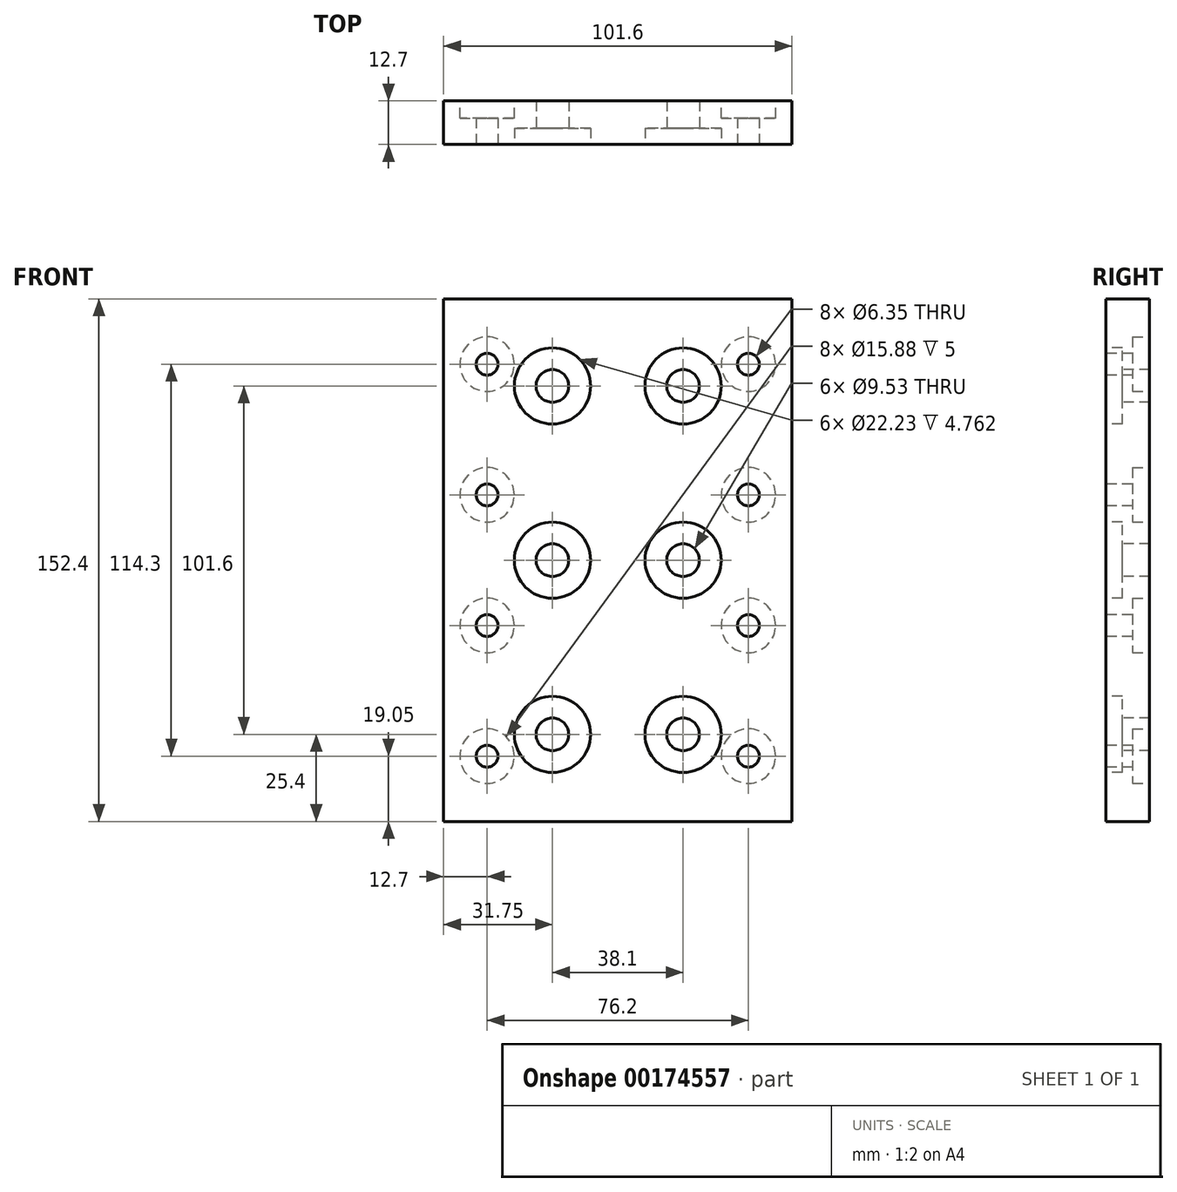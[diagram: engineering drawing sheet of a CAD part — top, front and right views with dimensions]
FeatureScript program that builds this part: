
annotation { "Feature Type Name" : "Feature", "Feature Type Description" : "" }
export const myFeature = defineFeature(function(context is Context, id is Id, definition is map)
    precondition{}
    {
        {
            var Q0;
            Q0=qCreatedBy(makeId("Front.planeOp"),FACE);
            var sketch = newSketch(context, id + "F0", { "sketchPlane" : qUnion([Q0])});
            skLineSegment(sketch, "E0.bottom", {"start": v(-50.8, -76.2) * mm, "end": v(50.8, -76.2) * mm});
            skLineSegment(sketch, "E0.top", {"start": v(-50.8, 76.2) * mm, "end": v(50.8, 76.2) * mm});
            skLineSegment(sketch, "E0.left", {"start": v(-50.8, -76.2) * mm, "end": v(-50.8, 76.2) * mm});
            skLineSegment(sketch, "E0.right", {"start": v(50.8, -76.2) * mm, "end": v(50.8, 76.2) * mm});
            skPoint(sketch, "E0.middle", {"position": v(0, 0) * mm});
            skSolve(sketch);
        }
        {
            var Q0;
            Q0 = qSketchRegion(id + "F0", true);
            extrude(context, id + "F1", {"entities" : qUnion([Q0]), "depth" : 12.7 * mm});
        }
        {
            var Q0;
            Q0=makeQuery(id+"F1.opExtrude","CAP_FACE",FACE,{"disambiguationData":[OSD([sQuery(id+"F0.wireOp",EDGE,"E0.bottom"),sQuery(id+"F0.wireOp",EDGE,"E0.top"),sQuery(id+"F0.wireOp",EDGE,"E0.left"),sQuery(id+"F0.wireOp",EDGE,"E0.right")])],"isStart":false});
            var sketch = newSketch(context, id + "F2", { "sketchPlane" : qUnion([Q0])});
            skLineSegment(sketch, "E1", {"start": v(-38.1, 57.15) * mm, "end": v(-50.8, 57.15) * mm, "construction": true});
            skCircle(sketch, "E2", {"center": v(-38.1, 57.15) * mm, "radius": 3.18 * mm});
            skCircle(sketch, "E3.0.1.0", {"center": v(-38.1, 19.05) * mm, "radius": 3.18 * mm});
            skCircle(sketch, "E3.0.2.0", {"center": v(-38.1, -19.05) * mm, "radius": 3.18 * mm});
            skCircle(sketch, "E3.0.3.0", {"center": v(-38.1, -57.15) * mm, "radius": 3.18 * mm});
            skCircle(sketch, "E3.1.0.0", {"center": v(38.1, 57.15) * mm, "radius": 3.18 * mm});
            skCircle(sketch, "E3.1.1.0", {"center": v(38.1, 19.05) * mm, "radius": 3.18 * mm});
            skCircle(sketch, "E3.1.2.0", {"center": v(38.1, -19.05) * mm, "radius": 3.18 * mm});
            skCircle(sketch, "E3.1.3.0", {"center": v(38.1, -57.15) * mm, "radius": 3.18 * mm});
            skLineSegment(sketch, "E3.direction1", {"start": v(-38.1, 57.15) * mm, "end": v(38.1, 57.15) * mm, "construction": true});
            skLineSegment(sketch, "E3.direction2", {"start": v(-38.1, 57.15) * mm, "end": v(-38.1, 19.05) * mm, "construction": true});
            skLineSegment(sketch, "E4", {"start": v(38.1, -57.15) * mm, "end": v(-38.1, -57.15) * mm, "construction": true});
            skLineSegment(sketch, "E5", {"start": v(0, -57.15) * mm, "end": v(0, -76.2) * mm, "construction": true});
            skLineSegment(sketch, "E6", {"start": v(0, 57.15) * mm, "end": v(0, 76.2) * mm, "construction": true});
            skSolve(sketch);
        }
        {
            var Q0;
            Q0 = qSketchRegion(id + "F2", true);
            extrude(context, id + "F3", {"entities" : qUnion([Q0]), "operationType" : NewBodyOperationType.REMOVE, "endBound" : BoundingType.THROUGH_ALL, "oppositeDirection" : true, "depth" : 25 * mm});
        }
        {
            var Q0;
            Q0=makeQuery(id+"F1.opExtrude","CAP_FACE",FACE,{"disambiguationData":[OSD([sQuery(id+"F0.wireOp",EDGE,"E0.bottom"),sQuery(id+"F0.wireOp",EDGE,"E0.top"),sQuery(id+"F0.wireOp",EDGE,"E0.left"),sQuery(id+"F0.wireOp",EDGE,"E0.right")])],"isStart":true});
            var sketch = newSketch(context, id + "F4", { "sketchPlane" : qUnion([Q0])});
            skCircle(sketch, "E7.0", {"center": v(-38.1, 57.15) * mm, "radius": 7.94 * mm});
            skCircle(sketch, "E8.0.1.0", {"center": v(-38.1, 19.05) * mm, "radius": 7.94 * mm});
            skCircle(sketch, "E8.0.2.0", {"center": v(-38.1, -19.05) * mm, "radius": 7.94 * mm});
            skCircle(sketch, "E8.0.3.0", {"center": v(-38.1, -57.15) * mm, "radius": 7.94 * mm});
            skCircle(sketch, "E8.1.0.0", {"center": v(38.1, 57.15) * mm, "radius": 7.94 * mm});
            skCircle(sketch, "E8.1.1.0", {"center": v(38.1, 19.05) * mm, "radius": 7.94 * mm});
            skCircle(sketch, "E8.1.2.0", {"center": v(38.1, -19.05) * mm, "radius": 7.94 * mm});
            skCircle(sketch, "E8.1.3.0", {"center": v(38.1, -57.15) * mm, "radius": 7.94 * mm});
            skLineSegment(sketch, "E8.direction1", {"start": v(-38.1, 57.15) * mm, "end": v(38.1, 57.15) * mm, "construction": true});
            skLineSegment(sketch, "E8.direction2", {"start": v(-38.1, 57.15) * mm, "end": v(-38.1, 19.05) * mm, "construction": true});
            skSolve(sketch);
        }
        {
            var Q0;
            Q0 = qSketchRegion(id + "F4", true);
            extrude(context, id + "F5", {"entities" : qUnion([Q0]), "operationType" : NewBodyOperationType.REMOVE, "oppositeDirection" : true, "depth" : 5 * mm});
        }
        {
            var Q0;
            Q0=makeQuery(id+"F1.opExtrude","CAP_FACE",FACE,{"disambiguationData":[OSD([sQuery(id+"F0.wireOp",EDGE,"E0.bottom"),sQuery(id+"F0.wireOp",EDGE,"E0.top"),sQuery(id+"F0.wireOp",EDGE,"E0.left"),sQuery(id+"F0.wireOp",EDGE,"E0.right")])],"isStart":false});
            var sketch = newSketch(context, id + "F6", { "sketchPlane" : qUnion([Q0])});
            skLineSegment(sketch, "E9", {"start": v(-19.05, 76.2) * mm, "end": v(-19.05, 50.8) * mm, "construction": true});
            skLineSegment(sketch, "E10", {"start": v(-19.05, 50.8) * mm, "end": v(-50.8, 50.8) * mm, "construction": true});
            skCircle(sketch, "E11", {"center": v(-19.05, 50.8) * mm, "radius": 4.76 * mm});
            skCircle(sketch, "E12.0.1.0", {"center": v(-19.05, 0) * mm, "radius": 4.76 * mm});
            skCircle(sketch, "E12.0.2.0", {"center": v(-19.05, -50.8) * mm, "radius": 4.76 * mm});
            skCircle(sketch, "E12.1.0.0", {"center": v(19.05, 50.8) * mm, "radius": 4.76 * mm});
            skCircle(sketch, "E12.1.1.0", {"center": v(19.05, 0) * mm, "radius": 4.76 * mm});
            skCircle(sketch, "E12.1.2.0", {"center": v(19.05, -50.8) * mm, "radius": 4.76 * mm});
            skLineSegment(sketch, "E12.direction1", {"start": v(-19.05, 50.8) * mm, "end": v(19.05, 50.8) * mm, "construction": true});
            skLineSegment(sketch, "E12.direction2", {"start": v(-19.05, 50.8) * mm, "end": v(-19.05, 0) * mm, "construction": true});
            skLineSegment(sketch, "E13", {"start": v(50.8, 0) * mm, "end": v(19.05, 0) * mm, "construction": true});
            skLineSegment(sketch, "E14", {"start": v(0, 50.8) * mm, "end": v(0, 76.2) * mm, "construction": true});
            skSolve(sketch);
        }
        {
            var Q0;
            Q0 = qSketchRegion(id + "F6", true);
            extrude(context, id + "F7", {"entities" : qUnion([Q0]), "operationType" : NewBodyOperationType.REMOVE, "endBound" : BoundingType.THROUGH_ALL, "oppositeDirection" : true, "depth" : 25 * mm});
        }
        {
            var Q0;
            Q0=makeQuery(id+"F1.opExtrude","CAP_FACE",FACE,{"disambiguationData":[OSD([sQuery(id+"F0.wireOp",EDGE,"E0.bottom"),sQuery(id+"F0.wireOp",EDGE,"E0.top"),sQuery(id+"F0.wireOp",EDGE,"E0.left"),sQuery(id+"F0.wireOp",EDGE,"E0.right")])],"isStart":false});
            var sketch = newSketch(context, id + "F8", { "sketchPlane" : qUnion([Q0])});
            skCircle(sketch, "E15.0", {"center": v(-19.05, 50.8) * mm, "radius": 11.11 * mm});
            skCircle(sketch, "E16.0.1.0", {"center": v(-19.05, 0) * mm, "radius": 11.11 * mm});
            skCircle(sketch, "E16.0.2.0", {"center": v(-19.05, -50.8) * mm, "radius": 11.11 * mm});
            skCircle(sketch, "E16.1.0.0", {"center": v(19.05, 50.8) * mm, "radius": 11.11 * mm});
            skCircle(sketch, "E16.1.1.0", {"center": v(19.05, 0) * mm, "radius": 11.11 * mm});
            skCircle(sketch, "E16.1.2.0", {"center": v(19.05, -50.8) * mm, "radius": 11.11 * mm});
            skLineSegment(sketch, "E16.direction1", {"start": v(-19.05, 50.8) * mm, "end": v(19.05, 50.8) * mm, "construction": true});
            skLineSegment(sketch, "E16.direction2", {"start": v(-19.05, 50.8) * mm, "end": v(-19.05, 0) * mm, "construction": true});
            skSolve(sketch);
        }
        {
            var Q0;
            Q0 = qSketchRegion(id + "F8", true);
            extrude(context, id + "F9", {"entities" : qUnion([Q0]), "operationType" : NewBodyOperationType.REMOVE, "oppositeDirection" : true, "depth" : 4.76 * mm});
        }
    });
